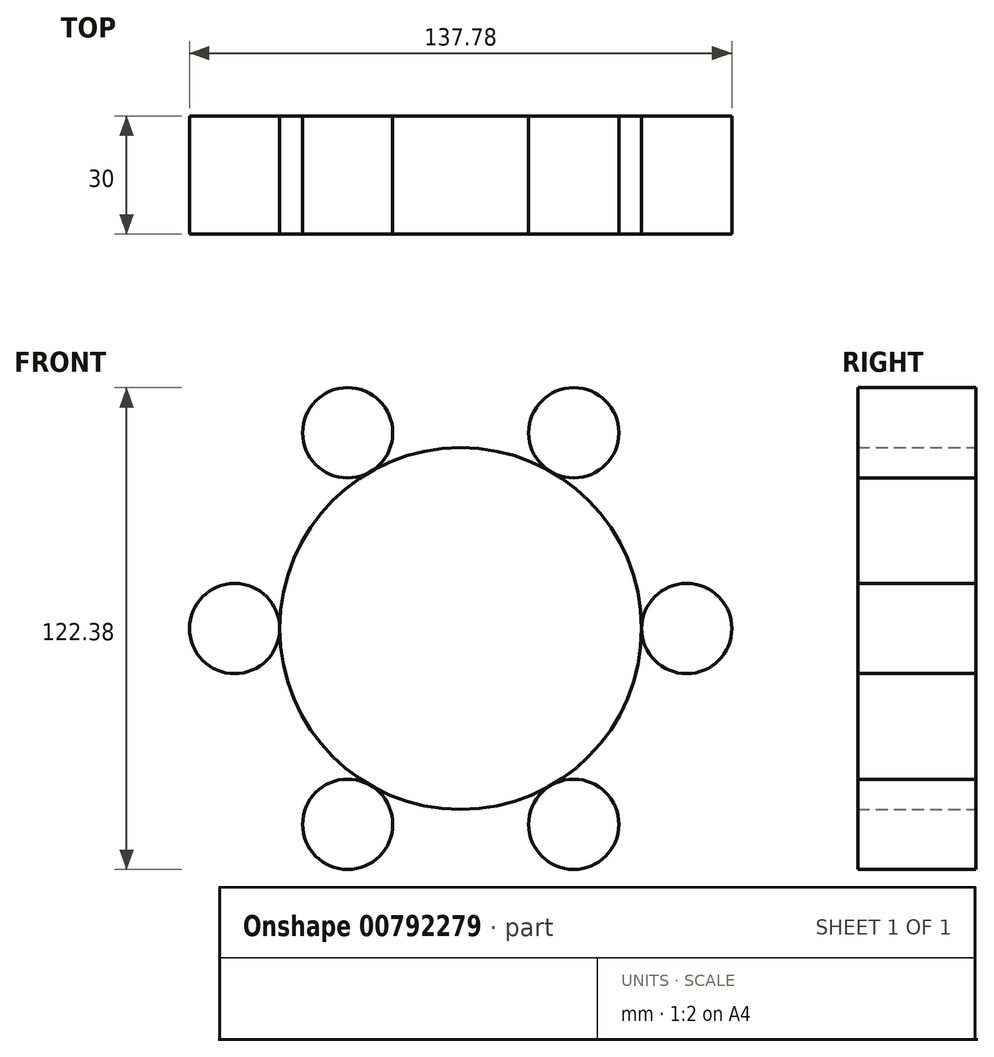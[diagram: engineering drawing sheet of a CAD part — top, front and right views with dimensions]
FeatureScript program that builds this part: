
annotation { "Feature Type Name" : "Feature", "Feature Type Description" : "" }
export const myFeature = defineFeature(function(context is Context, id is Id, definition is map)
    precondition{}
    {
        {
            var Q0;
            Q0=qCreatedBy(makeId("Front.planeOp"),FACE);
            var sketch = newSketch(context, id + "F0", { "sketchPlane" : qUnion([Q0])});
            skCircle(sketch, "E0", {"center": v(0, 0) * mm, "radius": 45.97 * mm});
            skCircle(sketch, "E1", {"center": v(-57.43, 0) * mm, "radius": 11.46 * mm});
            skSolve(sketch);
        }
        {
            var Q0;
            Q0=makeQuery(id+"F0.imprint","IMPRINT",FACE,{"disambiguationData":[TD([[makeQuery(id+"F0.imprint","IMPRINT",EDGE,{"derivedFrom":sQuery(id+"F0.wireOp",EDGE,"E1")}),1.0]])]});
            var Q1;
            Q1=makeQuery(id+"F0.imprint","IMPRINT",FACE,{"disambiguationData":[TD([[makeQuery(id+"F0.imprint","IMPRINT",EDGE,{"derivedFrom":sQuery(id+"F0.wireOp",EDGE,"E0")}),1.0]])]});
            extrude(context, id + "F1", {"entities" : qUnion([Q0, Q1]), "depth" : 30 * mm, "offsetDistance" : 25 * mm});
        }
        {
            var Q0;
            Q0=makeQuery(id+"F1.opExtrude","SWEPT_BODY",BODY,{"disambiguationData":[OSD([sQuery(id+"F0.wireOp",EDGE,"E1")])]});
            var Q1;
            Q1=makeQuery(id+"F1.opExtrude","CAP_EDGE",EDGE,{"disambiguationData":[OSD([sQuery(id+"F0.wireOp",EDGE,"E0")])],"isStart":false});
            circularPattern(context, id + "F2", {"entities" : qUnion([Q0]), "axis" : qUnion([Q1]), "angle" : 360 * degree, "instanceCount" : 6, "equalSpace" : true});
        }
    });
